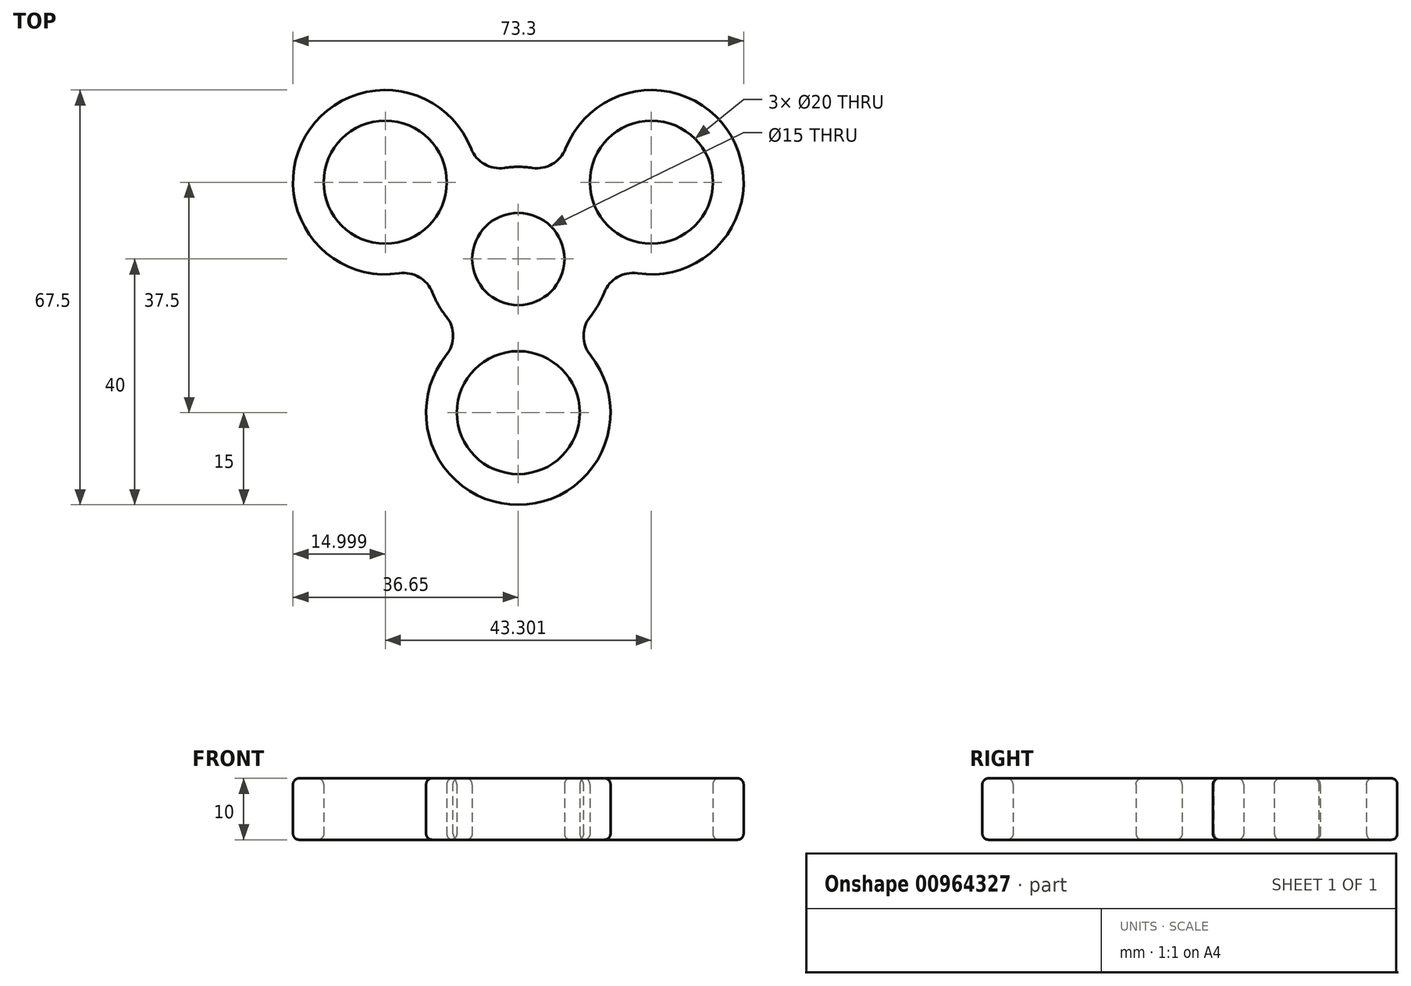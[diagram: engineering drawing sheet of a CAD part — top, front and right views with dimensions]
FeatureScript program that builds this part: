
annotation { "Feature Type Name" : "Feature", "Feature Type Description" : "" }
export const myFeature = defineFeature(function(context is Context, id is Id, definition is map)
    precondition{}
    {
        {
            var Q0;
            Q0=qCreatedBy(makeId("Top.planeOp"),FACE);
            var sketch = newSketch(context, id + "F0", { "sketchPlane" : qUnion([Q0])});
            skCircle(sketch, "E0", {"center": v(0, 0) * mm, "radius": 7.5 * mm});
            skCircle(sketch, "E1", {"center": v(0, 0) * mm, "radius": 15 * mm});
            skLineSegment(sketch, "E2", {"start": v(0, 0) * mm, "end": v(0, -25) * mm, "construction": true});
            skCircle(sketch, "E3", {"center": v(0, -25) * mm, "radius": 15 * mm});
            skCircle(sketch, "E4", {"center": v(0, -25) * mm, "radius": 10 * mm});
            skCircle(sketch, "E5.1.0", {"center": v(21.65, 12.5) * mm, "radius": 15 * mm});
            skCircle(sketch, "E5.1.1", {"center": v(21.65, 12.5) * mm, "radius": 10 * mm});
            skCircle(sketch, "E5.2.0", {"center": v(-21.65, 12.5) * mm, "radius": 15 * mm});
            skCircle(sketch, "E5.2.1", {"center": v(-21.65, 12.5) * mm, "radius": 10 * mm});
            skSolve(sketch);
        }
        {
            var Q0;
            {var subQ3=sQuery(id+"F0.wireOp",EDGE,"E5.2.1");Q0=makeQuery(id+"F0.imprint","IMPRINT",FACE,{"disambiguationData":[TD([[makeQuery(id+"F0.imprint","IMPRINT",EDGE,{"derivedFrom":subQ3}),-1.0]])]});}
            var Q1;
            Q1=makeQuery(id+"F0.imprint","IMPRINT",FACE,{"disambiguationData":[TD([[makeQuery(id+"F0.imprint","IMPRINT",EDGE,{"derivedFrom":sQuery(id+"F0.wireOp",EDGE,"E0")}),-1.0]])]});
            var Q2;
            {var subQ0=sQuery(id+"F0.wireOp",EDGE,"E5.2.0");var subQ1=sQuery(id+"F0.wireOp",EDGE,"E1");var subQ2=makeQuery(id+"F0.imprint","INTERSECT",VERTEX,{"disambiguationData":[OD(0.0)],"derivedFrom":[subQ1,subQ0]});Q2=makeQuery(id+"F0.imprint","IMPRINT",FACE,{"disambiguationData":[TD([[makeQuery(id+"F0.imprint","IMPRINT",EDGE,{"disambiguationData":[TD([[subQ2,-1.0]])],"derivedFrom":subQ1}),1.0]])]});}
            var Q3;
            {var subQ0=sQuery(id+"F0.wireOp",EDGE,"E5.1.0");var subQ1=sQuery(id+"F0.wireOp",EDGE,"E1");var subQ2=makeQuery(id+"F0.imprint","INTERSECT",VERTEX,{"disambiguationData":[OD(0.0)],"derivedFrom":[subQ1,subQ0]});Q3=makeQuery(id+"F0.imprint","IMPRINT",FACE,{"disambiguationData":[TD([[makeQuery(id+"F0.imprint","IMPRINT",EDGE,{"disambiguationData":[TD([[subQ2,1.0]])],"derivedFrom":subQ1}),1.0]])]});}
            var Q4;
            {var subQ3=sQuery(id+"F0.wireOp",EDGE,"E5.1.1");Q4=makeQuery(id+"F0.imprint","IMPRINT",FACE,{"disambiguationData":[TD([[makeQuery(id+"F0.imprint","IMPRINT",EDGE,{"derivedFrom":subQ3}),-1.0]])]});}
            var Q5;
            {var subQ0=sQuery(id+"F0.wireOp",EDGE,"E3");var subQ1=sQuery(id+"F0.wireOp",EDGE,"E1");var subQ2=makeQuery(id+"F0.imprint","INTERSECT",VERTEX,{"disambiguationData":[OD(0.0)],"derivedFrom":[subQ1,subQ0]});Q5=makeQuery(id+"F0.imprint","IMPRINT",FACE,{"disambiguationData":[TD([[makeQuery(id+"F0.imprint","IMPRINT",EDGE,{"disambiguationData":[TD([[subQ2,-1.0]])],"derivedFrom":subQ1}),1.0]])]});}
            var Q6;
            {var subQ3=sQuery(id+"F0.wireOp",EDGE,"E4");Q6=makeQuery(id+"F0.imprint","IMPRINT",FACE,{"disambiguationData":[TD([[makeQuery(id+"F0.imprint","IMPRINT",EDGE,{"derivedFrom":subQ3}),-1.0]])]});}
            extrude(context, id + "F1", {"entities" : qUnion([Q0, Q1, Q2, Q3, Q4, Q5, Q6]), "depth" : 10 * mm, "offsetDistance" : 25 * mm});
        }
        {
            var Q0;
            {var subQ0=sQuery(id+"F0.wireOp",EDGE,"E5.1.0");var subQ1=sQuery(id+"F0.wireOp",EDGE,"E1");Q0=makeQuery(id+"F1.opExtrude","SWEPT_EDGE",EDGE,{"disambiguationData":[OSD([subQ1,subQ0]),TDD([makeQuery(id+"F0.imprint","INTERSECT",VERTEX,{"disambiguationData":[OD(1.0)],"derivedFrom":[subQ1,subQ0]})])]});}
            var Q1;
            {var subQ0=sQuery(id+"F0.wireOp",EDGE,"E3");var subQ1=sQuery(id+"F0.wireOp",EDGE,"E1");Q1=makeQuery(id+"F1.opExtrude","SWEPT_EDGE",EDGE,{"disambiguationData":[OSD([subQ1,subQ0]),TDD([makeQuery(id+"F0.imprint","INTERSECT",VERTEX,{"disambiguationData":[OD(1.0)],"derivedFrom":[subQ1,subQ0]})])]});}
            var Q2;
            {var subQ0=sQuery(id+"F0.wireOp",EDGE,"E3");var subQ1=sQuery(id+"F0.wireOp",EDGE,"E1");Q2=makeQuery(id+"F1.opExtrude","SWEPT_EDGE",EDGE,{"disambiguationData":[OSD([subQ1,subQ0]),TDD([makeQuery(id+"F0.imprint","INTERSECT",VERTEX,{"disambiguationData":[OD(0.0)],"derivedFrom":[subQ1,subQ0]})])]});}
            var Q3;
            {var subQ0=sQuery(id+"F0.wireOp",EDGE,"E5.2.0");var subQ1=sQuery(id+"F0.wireOp",EDGE,"E1");Q3=makeQuery(id+"F1.opExtrude","SWEPT_EDGE",EDGE,{"disambiguationData":[OSD([subQ1,subQ0]),TDD([makeQuery(id+"F0.imprint","INTERSECT",VERTEX,{"disambiguationData":[OD(1.0)],"derivedFrom":[subQ1,subQ0]})])]});}
            var Q4;
            {var subQ0=sQuery(id+"F0.wireOp",EDGE,"E5.2.0");var subQ1=sQuery(id+"F0.wireOp",EDGE,"E1");Q4=makeQuery(id+"F1.opExtrude","SWEPT_EDGE",EDGE,{"disambiguationData":[OSD([subQ1,subQ0]),TDD([makeQuery(id+"F0.imprint","INTERSECT",VERTEX,{"disambiguationData":[OD(0.0)],"derivedFrom":[subQ1,subQ0]})])]});}
            var Q5;
            {var subQ0=sQuery(id+"F0.wireOp",EDGE,"E5.1.0");var subQ1=sQuery(id+"F0.wireOp",EDGE,"E1");Q5=makeQuery(id+"F1.opExtrude","SWEPT_EDGE",EDGE,{"disambiguationData":[OSD([subQ1,subQ0]),TDD([makeQuery(id+"F0.imprint","INTERSECT",VERTEX,{"disambiguationData":[OD(0.0)],"derivedFrom":[subQ1,subQ0]})])]});}
            fillet(context, id + "F2", {"entities" : qUnion([Q0, Q1, Q2, Q3, Q4, Q5]), "radius" : 5 * mm, "tangentPropagation" : true, "allowEdgeOverflow" : false});
        }
        {
            var Q0;
            Q0=makeQuery(id+"F1.opExtrude","CAP_EDGE",EDGE,{"disambiguationData":[OSD([sQuery(id+"F0.wireOp",EDGE,"E3")])],"isStart":true});
            var Q1;
            Q1=makeQuery(id+"F1.opExtrude","CAP_EDGE",EDGE,{"disambiguationData":[OSD([sQuery(id+"F0.wireOp",EDGE,"E5.1.0")])],"isStart":true});
            var Q2;
            Q2=makeQuery(id+"F1.opExtrude","CAP_EDGE",EDGE,{"disambiguationData":[OSD([sQuery(id+"F0.wireOp",EDGE,"E5.1.0")])],"isStart":false});
            var Q3;
            Q3=makeQuery(id+"F1.opExtrude","CAP_EDGE",EDGE,{"disambiguationData":[OSD([sQuery(id+"F0.wireOp",EDGE,"E5.2.0")])],"isStart":true});
            var Q4;
            Q4=makeQuery(id+"F1.opExtrude","CAP_EDGE",EDGE,{"disambiguationData":[OSD([sQuery(id+"F0.wireOp",EDGE,"E5.2.0")])],"isStart":false});
            var Q5;
            {var subQ0=sQuery(id+"F0.wireOp",EDGE,"E1");Q5=makeQuery(id+"F1.opExtrude","CAP_EDGE",EDGE,{"disambiguationData":[OSD([subQ0]),TDD([makeQuery(id+"F0.imprint","IMPRINT",EDGE,{"disambiguationData":[TD([[makeQuery(id+"F0.imprint","INTERSECT",VERTEX,{"disambiguationData":[OD(1.0)],"derivedFrom":[subQ0,sQuery(id+"F0.wireOp",EDGE,"E3")]}),-1.0]])],"derivedFrom":subQ0})])],"isStart":true});}
            var Q6;
            Q6=makeQuery(id+"F1.opExtrude","CAP_EDGE",EDGE,{"disambiguationData":[OSD([sQuery(id+"F0.wireOp",EDGE,"E5.2.1")])],"isStart":false});
            var Q7;
            Q7=makeQuery(id+"F1.opExtrude","CAP_EDGE",EDGE,{"disambiguationData":[OSD([sQuery(id+"F0.wireOp",EDGE,"E5.2.1")])],"isStart":true});
            var Q8;
            Q8=makeQuery(id+"F1.opExtrude","CAP_EDGE",EDGE,{"disambiguationData":[OSD([sQuery(id+"F0.wireOp",EDGE,"E4")])],"isStart":false});
            var Q9;
            Q9=makeQuery(id+"F1.opExtrude","CAP_EDGE",EDGE,{"disambiguationData":[OSD([sQuery(id+"F0.wireOp",EDGE,"E5.1.1")])],"isStart":true});
            var Q10;
            {var subQ0=sQuery(id+"F0.wireOp",EDGE,"E1");Q10=makeQuery(id+"F1.opExtrude","CAP_EDGE",EDGE,{"disambiguationData":[OSD([subQ0]),TDD([makeQuery(id+"F0.imprint","IMPRINT",EDGE,{"disambiguationData":[TD([[makeQuery(id+"F0.imprint","INTERSECT",VERTEX,{"disambiguationData":[OD(1.0)],"derivedFrom":[subQ0,sQuery(id+"F0.wireOp",EDGE,"E3")]}),-1.0]])],"derivedFrom":subQ0})])],"isStart":false});}
            var Q11;
            Q11=makeQuery(id+"F1.opExtrude","CAP_EDGE",EDGE,{"disambiguationData":[OSD([sQuery(id+"F0.wireOp",EDGE,"E5.1.1")])],"isStart":false});
            var Q12;
            Q12=makeQuery(id+"F1.opExtrude","CAP_EDGE",EDGE,{"disambiguationData":[OSD([sQuery(id+"F0.wireOp",EDGE,"E3")])],"isStart":false});
            var Q13;
            {var subQ0=sQuery(id+"F0.wireOp",EDGE,"E5.2.0");var subQ1=sQuery(id+"F0.wireOp",EDGE,"E1");Q13=makeQuery(id+"F2.opFillet","BLEND_EDGE",EDGE,{"blendedFrom":[makeQuery(id+"F1.opExtrude","SWEPT_EDGE",EDGE,{"disambiguationData":[OSD([subQ1,subQ0]),TDD([makeQuery(id+"F0.imprint","INTERSECT",VERTEX,{"disambiguationData":[OD(1.0)],"derivedFrom":[subQ1,subQ0]})])]}),makeQuery(id+"F1.opExtrude","SWEPT_FACE",FACE,{"disambiguationData":[OSD([subQ0])]})],"blendedInto":[makeQuery(id+"F1.opExtrude","SWEPT_FACE",FACE,{"disambiguationData":[OSD([subQ0])]})]});}
            var Q14;
            {var subQ0=sQuery(id+"F0.wireOp",EDGE,"E3");var subQ1=sQuery(id+"F0.wireOp",EDGE,"E1");Q14=makeQuery(id+"F2.opFillet","BLEND_EDGE",EDGE,{"blendedFrom":[makeQuery(id+"F1.opExtrude","SWEPT_EDGE",EDGE,{"disambiguationData":[OSD([subQ1,subQ0]),TDD([makeQuery(id+"F0.imprint","INTERSECT",VERTEX,{"disambiguationData":[OD(1.0)],"derivedFrom":[subQ1,subQ0]})])]}),makeQuery(id+"F1.opExtrude","CAP_FACE",FACE,{"disambiguationData":[OSD([sQuery(id+"F0.wireOp",EDGE,"E0"),subQ1,subQ0,sQuery(id+"F0.wireOp",EDGE,"E4"),sQuery(id+"F0.wireOp",EDGE,"E5.1.0"),sQuery(id+"F0.wireOp",EDGE,"E5.1.1"),sQuery(id+"F0.wireOp",EDGE,"E5.2.0"),sQuery(id+"F0.wireOp",EDGE,"E5.2.1")])],"isStart":true})],"blendedInto":[makeQuery(id+"F1.opExtrude","CAP_FACE",FACE,{"disambiguationData":[OSD([sQuery(id+"F0.wireOp",EDGE,"E0"),subQ1,subQ0,sQuery(id+"F0.wireOp",EDGE,"E4"),sQuery(id+"F0.wireOp",EDGE,"E5.1.0"),sQuery(id+"F0.wireOp",EDGE,"E5.1.1"),sQuery(id+"F0.wireOp",EDGE,"E5.2.0"),sQuery(id+"F0.wireOp",EDGE,"E5.2.1")])],"isStart":true})]});}
            var Q15;
            {var subQ0=sQuery(id+"F0.wireOp",EDGE,"E3");var subQ1=sQuery(id+"F0.wireOp",EDGE,"E1");Q15=makeQuery(id+"F2.opFillet","BLEND_EDGE",EDGE,{"blendedFrom":[makeQuery(id+"F1.opExtrude","SWEPT_EDGE",EDGE,{"disambiguationData":[OSD([subQ1,subQ0]),TDD([makeQuery(id+"F0.imprint","INTERSECT",VERTEX,{"disambiguationData":[OD(1.0)],"derivedFrom":[subQ1,subQ0]})])]}),makeQuery(id+"F1.opExtrude","CAP_FACE",FACE,{"disambiguationData":[OSD([sQuery(id+"F0.wireOp",EDGE,"E0"),subQ1,subQ0,sQuery(id+"F0.wireOp",EDGE,"E4"),sQuery(id+"F0.wireOp",EDGE,"E5.1.0"),sQuery(id+"F0.wireOp",EDGE,"E5.1.1"),sQuery(id+"F0.wireOp",EDGE,"E5.2.0"),sQuery(id+"F0.wireOp",EDGE,"E5.2.1")])],"isStart":false})],"blendedInto":[makeQuery(id+"F1.opExtrude","CAP_FACE",FACE,{"disambiguationData":[OSD([sQuery(id+"F0.wireOp",EDGE,"E0"),subQ1,subQ0,sQuery(id+"F0.wireOp",EDGE,"E4"),sQuery(id+"F0.wireOp",EDGE,"E5.1.0"),sQuery(id+"F0.wireOp",EDGE,"E5.1.1"),sQuery(id+"F0.wireOp",EDGE,"E5.2.0"),sQuery(id+"F0.wireOp",EDGE,"E5.2.1")])],"isStart":false})]});}
            var Q16;
            {var subQ0=sQuery(id+"F0.wireOp",EDGE,"E3");var subQ1=sQuery(id+"F0.wireOp",EDGE,"E1");var subQ2=makeQuery(id+"F0.imprint","INTERSECT",VERTEX,{"disambiguationData":[OD(1.0)],"derivedFrom":[subQ1,subQ0]});Q16=makeQuery(id+"F2.opFillet","BLEND_EDGE",EDGE,{"blendedFrom":[makeQuery(id+"F1.opExtrude","SWEPT_EDGE",EDGE,{"disambiguationData":[OSD([subQ1,subQ0]),TDD([subQ2])]}),makeQuery(id+"F1.opExtrude","SWEPT_FACE",FACE,{"disambiguationData":[OSD([subQ1]),TDD([makeQuery(id+"F0.imprint","IMPRINT",EDGE,{"disambiguationData":[TD([[subQ2,-1.0]])],"derivedFrom":subQ1})])]})],"blendedInto":[makeQuery(id+"F1.opExtrude","SWEPT_FACE",FACE,{"disambiguationData":[OSD([subQ1]),TDD([makeQuery(id+"F0.imprint","IMPRINT",EDGE,{"disambiguationData":[TD([[subQ2,-1.0]])],"derivedFrom":subQ1})])]})]});}
            var Q17;
            {var subQ0=sQuery(id+"F0.wireOp",EDGE,"E3");var subQ1=sQuery(id+"F0.wireOp",EDGE,"E1");Q17=makeQuery(id+"F2.opFillet","BLEND_EDGE",EDGE,{"blendedFrom":[makeQuery(id+"F1.opExtrude","SWEPT_EDGE",EDGE,{"disambiguationData":[OSD([subQ1,subQ0]),TDD([makeQuery(id+"F0.imprint","INTERSECT",VERTEX,{"disambiguationData":[OD(1.0)],"derivedFrom":[subQ1,subQ0]})])]}),makeQuery(id+"F1.opExtrude","SWEPT_FACE",FACE,{"disambiguationData":[OSD([subQ0])]})],"blendedInto":[makeQuery(id+"F1.opExtrude","SWEPT_FACE",FACE,{"disambiguationData":[OSD([subQ0])]})]});}
            var Q18;
            {var subQ0=sQuery(id+"F0.wireOp",EDGE,"E5.1.0");var subQ1=sQuery(id+"F0.wireOp",EDGE,"E1");Q18=makeQuery(id+"F2.opFillet","BLEND_EDGE",EDGE,{"blendedFrom":[makeQuery(id+"F1.opExtrude","SWEPT_EDGE",EDGE,{"disambiguationData":[OSD([subQ1,subQ0]),TDD([makeQuery(id+"F0.imprint","INTERSECT",VERTEX,{"disambiguationData":[OD(1.0)],"derivedFrom":[subQ1,subQ0]})])]}),makeQuery(id+"F1.opExtrude","CAP_FACE",FACE,{"disambiguationData":[OSD([sQuery(id+"F0.wireOp",EDGE,"E0"),subQ1,sQuery(id+"F0.wireOp",EDGE,"E3"),sQuery(id+"F0.wireOp",EDGE,"E4"),subQ0,sQuery(id+"F0.wireOp",EDGE,"E5.1.1"),sQuery(id+"F0.wireOp",EDGE,"E5.2.0"),sQuery(id+"F0.wireOp",EDGE,"E5.2.1")])],"isStart":true})],"blendedInto":[makeQuery(id+"F1.opExtrude","CAP_FACE",FACE,{"disambiguationData":[OSD([sQuery(id+"F0.wireOp",EDGE,"E0"),subQ1,sQuery(id+"F0.wireOp",EDGE,"E3"),sQuery(id+"F0.wireOp",EDGE,"E4"),subQ0,sQuery(id+"F0.wireOp",EDGE,"E5.1.1"),sQuery(id+"F0.wireOp",EDGE,"E5.2.0"),sQuery(id+"F0.wireOp",EDGE,"E5.2.1")])],"isStart":true})]});}
            var Q19;
            {var subQ0=sQuery(id+"F0.wireOp",EDGE,"E1");var subQ1=sQuery(id+"F0.wireOp",EDGE,"E5.1.0");var subQ2=makeQuery(id+"F0.imprint","INTERSECT",VERTEX,{"disambiguationData":[OD(1.0)],"derivedFrom":[subQ0,subQ1]});Q19=makeQuery(id+"F2.opFillet","BLEND_EDGE",EDGE,{"blendedFrom":[makeQuery(id+"F1.opExtrude","SWEPT_EDGE",EDGE,{"disambiguationData":[OSD([subQ0,subQ1]),TDD([subQ2])]}),makeQuery(id+"F1.opExtrude","SWEPT_FACE",FACE,{"disambiguationData":[OSD([subQ0]),TDD([makeQuery(id+"F0.imprint","IMPRINT",EDGE,{"disambiguationData":[TD([[makeQuery(id+"F0.imprint","INTERSECT",VERTEX,{"disambiguationData":[OD(1.0)],"derivedFrom":[subQ0,sQuery(id+"F0.wireOp",EDGE,"E3")]}),-1.0]])],"derivedFrom":subQ0})])]})],"blendedInto":[makeQuery(id+"F1.opExtrude","SWEPT_FACE",FACE,{"disambiguationData":[OSD([subQ0]),TDD([makeQuery(id+"F0.imprint","IMPRINT",EDGE,{"disambiguationData":[TD([[makeQuery(id+"F0.imprint","INTERSECT",VERTEX,{"disambiguationData":[OD(1.0)],"derivedFrom":[subQ0,sQuery(id+"F0.wireOp",EDGE,"E3")]}),-1.0]])],"derivedFrom":subQ0})])]})]});}
            var Q20;
            {var subQ0=sQuery(id+"F0.wireOp",EDGE,"E5.1.0");var subQ1=sQuery(id+"F0.wireOp",EDGE,"E1");Q20=makeQuery(id+"F2.opFillet","BLEND_EDGE",EDGE,{"blendedFrom":[makeQuery(id+"F1.opExtrude","SWEPT_EDGE",EDGE,{"disambiguationData":[OSD([subQ1,subQ0]),TDD([makeQuery(id+"F0.imprint","INTERSECT",VERTEX,{"disambiguationData":[OD(1.0)],"derivedFrom":[subQ1,subQ0]})])]}),makeQuery(id+"F1.opExtrude","SWEPT_FACE",FACE,{"disambiguationData":[OSD([subQ0])]})],"blendedInto":[makeQuery(id+"F1.opExtrude","SWEPT_FACE",FACE,{"disambiguationData":[OSD([subQ0])]})]});}
            var Q21;
            {var subQ0=sQuery(id+"F0.wireOp",EDGE,"E1");Q21=makeQuery(id+"F1.opExtrude","CAP_EDGE",EDGE,{"disambiguationData":[OSD([subQ0]),TDD([makeQuery(id+"F0.imprint","IMPRINT",EDGE,{"disambiguationData":[TD([[makeQuery(id+"F0.imprint","INTERSECT",VERTEX,{"disambiguationData":[OD(0.0)],"derivedFrom":[subQ0,sQuery(id+"F0.wireOp",EDGE,"E5.1.0")]}),-1.0]])],"derivedFrom":subQ0})])],"isStart":true});}
            var Q22;
            Q22=makeQuery(id+"F1.opExtrude","CAP_EDGE",EDGE,{"disambiguationData":[OSD([sQuery(id+"F0.wireOp",EDGE,"E0")])],"isStart":false});
            var Q23;
            {var subQ0=sQuery(id+"F0.wireOp",EDGE,"E5.2.0");var subQ1=sQuery(id+"F0.wireOp",EDGE,"E1");Q23=makeQuery(id+"F2.opFillet","BLEND_EDGE",EDGE,{"blendedFrom":[makeQuery(id+"F1.opExtrude","SWEPT_EDGE",EDGE,{"disambiguationData":[OSD([subQ1,subQ0]),TDD([makeQuery(id+"F0.imprint","INTERSECT",VERTEX,{"disambiguationData":[OD(0.0)],"derivedFrom":[subQ1,subQ0]})])]}),makeQuery(id+"F1.opExtrude","SWEPT_FACE",FACE,{"disambiguationData":[OSD([subQ0])]})],"blendedInto":[makeQuery(id+"F1.opExtrude","SWEPT_FACE",FACE,{"disambiguationData":[OSD([subQ0])]})]});}
            var Q24;
            {var subQ0=sQuery(id+"F0.wireOp",EDGE,"E5.2.0");var subQ1=sQuery(id+"F0.wireOp",EDGE,"E1");Q24=makeQuery(id+"F2.opFillet","BLEND_EDGE",EDGE,{"blendedFrom":[makeQuery(id+"F1.opExtrude","SWEPT_EDGE",EDGE,{"disambiguationData":[OSD([subQ1,subQ0]),TDD([makeQuery(id+"F0.imprint","INTERSECT",VERTEX,{"disambiguationData":[OD(1.0)],"derivedFrom":[subQ1,subQ0]})])]}),makeQuery(id+"F1.opExtrude","CAP_FACE",FACE,{"disambiguationData":[OSD([sQuery(id+"F0.wireOp",EDGE,"E0"),subQ1,sQuery(id+"F0.wireOp",EDGE,"E3"),sQuery(id+"F0.wireOp",EDGE,"E4"),sQuery(id+"F0.wireOp",EDGE,"E5.1.0"),sQuery(id+"F0.wireOp",EDGE,"E5.1.1"),subQ0,sQuery(id+"F0.wireOp",EDGE,"E5.2.1")])],"isStart":false})],"blendedInto":[makeQuery(id+"F1.opExtrude","CAP_FACE",FACE,{"disambiguationData":[OSD([sQuery(id+"F0.wireOp",EDGE,"E0"),subQ1,sQuery(id+"F0.wireOp",EDGE,"E3"),sQuery(id+"F0.wireOp",EDGE,"E4"),sQuery(id+"F0.wireOp",EDGE,"E5.1.0"),sQuery(id+"F0.wireOp",EDGE,"E5.1.1"),subQ0,sQuery(id+"F0.wireOp",EDGE,"E5.2.1")])],"isStart":false})]});}
            var Q25;
            {var subQ0=sQuery(id+"F0.wireOp",EDGE,"E5.1.0");var subQ1=sQuery(id+"F0.wireOp",EDGE,"E1");Q25=makeQuery(id+"F2.opFillet","BLEND_EDGE",EDGE,{"blendedFrom":[makeQuery(id+"F1.opExtrude","SWEPT_EDGE",EDGE,{"disambiguationData":[OSD([subQ1,subQ0]),TDD([makeQuery(id+"F0.imprint","INTERSECT",VERTEX,{"disambiguationData":[OD(0.0)],"derivedFrom":[subQ1,subQ0]})])]}),makeQuery(id+"F1.opExtrude","CAP_FACE",FACE,{"disambiguationData":[OSD([sQuery(id+"F0.wireOp",EDGE,"E0"),subQ1,sQuery(id+"F0.wireOp",EDGE,"E3"),sQuery(id+"F0.wireOp",EDGE,"E4"),subQ0,sQuery(id+"F0.wireOp",EDGE,"E5.1.1"),sQuery(id+"F0.wireOp",EDGE,"E5.2.0"),sQuery(id+"F0.wireOp",EDGE,"E5.2.1")])],"isStart":true})],"blendedInto":[makeQuery(id+"F1.opExtrude","CAP_FACE",FACE,{"disambiguationData":[OSD([sQuery(id+"F0.wireOp",EDGE,"E0"),subQ1,sQuery(id+"F0.wireOp",EDGE,"E3"),sQuery(id+"F0.wireOp",EDGE,"E4"),subQ0,sQuery(id+"F0.wireOp",EDGE,"E5.1.1"),sQuery(id+"F0.wireOp",EDGE,"E5.2.0"),sQuery(id+"F0.wireOp",EDGE,"E5.2.1")])],"isStart":true})]});}
            var Q26;
            {var subQ0=sQuery(id+"F0.wireOp",EDGE,"E3");var subQ1=sQuery(id+"F0.wireOp",EDGE,"E1");Q26=makeQuery(id+"F2.opFillet","BLEND_EDGE",EDGE,{"blendedFrom":[makeQuery(id+"F1.opExtrude","SWEPT_EDGE",EDGE,{"disambiguationData":[OSD([subQ1,subQ0]),TDD([makeQuery(id+"F0.imprint","INTERSECT",VERTEX,{"disambiguationData":[OD(0.0)],"derivedFrom":[subQ1,subQ0]})])]}),makeQuery(id+"F1.opExtrude","SWEPT_FACE",FACE,{"disambiguationData":[OSD([subQ0])]})],"blendedInto":[makeQuery(id+"F1.opExtrude","SWEPT_FACE",FACE,{"disambiguationData":[OSD([subQ0])]})]});}
            var Q27;
            {var subQ0=sQuery(id+"F0.wireOp",EDGE,"E3");var subQ1=sQuery(id+"F0.wireOp",EDGE,"E1");Q27=makeQuery(id+"F2.opFillet","BLEND_EDGE",EDGE,{"blendedFrom":[makeQuery(id+"F1.opExtrude","SWEPT_EDGE",EDGE,{"disambiguationData":[OSD([subQ1,subQ0]),TDD([makeQuery(id+"F0.imprint","INTERSECT",VERTEX,{"disambiguationData":[OD(0.0)],"derivedFrom":[subQ1,subQ0]})])]}),makeQuery(id+"F1.opExtrude","CAP_FACE",FACE,{"disambiguationData":[OSD([sQuery(id+"F0.wireOp",EDGE,"E0"),subQ1,subQ0,sQuery(id+"F0.wireOp",EDGE,"E4"),sQuery(id+"F0.wireOp",EDGE,"E5.1.0"),sQuery(id+"F0.wireOp",EDGE,"E5.1.1"),sQuery(id+"F0.wireOp",EDGE,"E5.2.0"),sQuery(id+"F0.wireOp",EDGE,"E5.2.1")])],"isStart":true})],"blendedInto":[makeQuery(id+"F1.opExtrude","CAP_FACE",FACE,{"disambiguationData":[OSD([sQuery(id+"F0.wireOp",EDGE,"E0"),subQ1,subQ0,sQuery(id+"F0.wireOp",EDGE,"E4"),sQuery(id+"F0.wireOp",EDGE,"E5.1.0"),sQuery(id+"F0.wireOp",EDGE,"E5.1.1"),sQuery(id+"F0.wireOp",EDGE,"E5.2.0"),sQuery(id+"F0.wireOp",EDGE,"E5.2.1")])],"isStart":true})]});}
            var Q28;
            {var subQ0=sQuery(id+"F0.wireOp",EDGE,"E5.2.0");var subQ1=sQuery(id+"F0.wireOp",EDGE,"E1");Q28=makeQuery(id+"F2.opFillet","BLEND_EDGE",EDGE,{"blendedFrom":[makeQuery(id+"F1.opExtrude","SWEPT_EDGE",EDGE,{"disambiguationData":[OSD([subQ1,subQ0]),TDD([makeQuery(id+"F0.imprint","INTERSECT",VERTEX,{"disambiguationData":[OD(0.0)],"derivedFrom":[subQ1,subQ0]})])]}),makeQuery(id+"F1.opExtrude","CAP_FACE",FACE,{"disambiguationData":[OSD([sQuery(id+"F0.wireOp",EDGE,"E0"),subQ1,sQuery(id+"F0.wireOp",EDGE,"E3"),sQuery(id+"F0.wireOp",EDGE,"E4"),sQuery(id+"F0.wireOp",EDGE,"E5.1.0"),sQuery(id+"F0.wireOp",EDGE,"E5.1.1"),subQ0,sQuery(id+"F0.wireOp",EDGE,"E5.2.1")])],"isStart":false})],"blendedInto":[makeQuery(id+"F1.opExtrude","CAP_FACE",FACE,{"disambiguationData":[OSD([sQuery(id+"F0.wireOp",EDGE,"E0"),subQ1,sQuery(id+"F0.wireOp",EDGE,"E3"),sQuery(id+"F0.wireOp",EDGE,"E4"),sQuery(id+"F0.wireOp",EDGE,"E5.1.0"),sQuery(id+"F0.wireOp",EDGE,"E5.1.1"),subQ0,sQuery(id+"F0.wireOp",EDGE,"E5.2.1")])],"isStart":false})]});}
            var Q29;
            Q29=makeQuery(id+"F1.opExtrude","CAP_EDGE",EDGE,{"disambiguationData":[OSD([sQuery(id+"F0.wireOp",EDGE,"E0")])],"isStart":true});
            var Q30;
            Q30=makeQuery(id+"F1.opExtrude","CAP_EDGE",EDGE,{"disambiguationData":[OSD([sQuery(id+"F0.wireOp",EDGE,"E4")])],"isStart":true});
            var Q31;
            {var subQ0=sQuery(id+"F0.wireOp",EDGE,"E1");Q31=makeQuery(id+"F1.opExtrude","CAP_EDGE",EDGE,{"disambiguationData":[OSD([subQ0]),TDD([makeQuery(id+"F0.imprint","IMPRINT",EDGE,{"disambiguationData":[TD([[makeQuery(id+"F0.imprint","INTERSECT",VERTEX,{"disambiguationData":[OD(0.0)],"derivedFrom":[subQ0,sQuery(id+"F0.wireOp",EDGE,"E5.1.0")]}),-1.0]])],"derivedFrom":subQ0})])],"isStart":false});}
            var Q32;
            {var subQ0=sQuery(id+"F0.wireOp",EDGE,"E5.1.0");var subQ1=sQuery(id+"F0.wireOp",EDGE,"E1");Q32=makeQuery(id+"F2.opFillet","BLEND_EDGE",EDGE,{"blendedFrom":[makeQuery(id+"F1.opExtrude","SWEPT_EDGE",EDGE,{"disambiguationData":[OSD([subQ1,subQ0]),TDD([makeQuery(id+"F0.imprint","INTERSECT",VERTEX,{"disambiguationData":[OD(1.0)],"derivedFrom":[subQ1,subQ0]})])]}),makeQuery(id+"F1.opExtrude","CAP_FACE",FACE,{"disambiguationData":[OSD([sQuery(id+"F0.wireOp",EDGE,"E0"),subQ1,sQuery(id+"F0.wireOp",EDGE,"E3"),sQuery(id+"F0.wireOp",EDGE,"E4"),subQ0,sQuery(id+"F0.wireOp",EDGE,"E5.1.1"),sQuery(id+"F0.wireOp",EDGE,"E5.2.0"),sQuery(id+"F0.wireOp",EDGE,"E5.2.1")])],"isStart":false})],"blendedInto":[makeQuery(id+"F1.opExtrude","CAP_FACE",FACE,{"disambiguationData":[OSD([sQuery(id+"F0.wireOp",EDGE,"E0"),subQ1,sQuery(id+"F0.wireOp",EDGE,"E3"),sQuery(id+"F0.wireOp",EDGE,"E4"),subQ0,sQuery(id+"F0.wireOp",EDGE,"E5.1.1"),sQuery(id+"F0.wireOp",EDGE,"E5.2.0"),sQuery(id+"F0.wireOp",EDGE,"E5.2.1")])],"isStart":false})]});}
            var Q33;
            {var subQ0=sQuery(id+"F0.wireOp",EDGE,"E3");var subQ1=sQuery(id+"F0.wireOp",EDGE,"E1");Q33=makeQuery(id+"F2.opFillet","BLEND_EDGE",EDGE,{"blendedFrom":[makeQuery(id+"F1.opExtrude","SWEPT_EDGE",EDGE,{"disambiguationData":[OSD([subQ1,subQ0]),TDD([makeQuery(id+"F0.imprint","INTERSECT",VERTEX,{"disambiguationData":[OD(0.0)],"derivedFrom":[subQ1,subQ0]})])]}),makeQuery(id+"F1.opExtrude","CAP_FACE",FACE,{"disambiguationData":[OSD([sQuery(id+"F0.wireOp",EDGE,"E0"),subQ1,subQ0,sQuery(id+"F0.wireOp",EDGE,"E4"),sQuery(id+"F0.wireOp",EDGE,"E5.1.0"),sQuery(id+"F0.wireOp",EDGE,"E5.1.1"),sQuery(id+"F0.wireOp",EDGE,"E5.2.0"),sQuery(id+"F0.wireOp",EDGE,"E5.2.1")])],"isStart":false})],"blendedInto":[makeQuery(id+"F1.opExtrude","CAP_FACE",FACE,{"disambiguationData":[OSD([sQuery(id+"F0.wireOp",EDGE,"E0"),subQ1,subQ0,sQuery(id+"F0.wireOp",EDGE,"E4"),sQuery(id+"F0.wireOp",EDGE,"E5.1.0"),sQuery(id+"F0.wireOp",EDGE,"E5.1.1"),sQuery(id+"F0.wireOp",EDGE,"E5.2.0"),sQuery(id+"F0.wireOp",EDGE,"E5.2.1")])],"isStart":false})]});}
            var Q34;
            {var subQ0=sQuery(id+"F0.wireOp",EDGE,"E5.1.0");var subQ1=sQuery(id+"F0.wireOp",EDGE,"E1");Q34=makeQuery(id+"F2.opFillet","BLEND_EDGE",EDGE,{"blendedFrom":[makeQuery(id+"F1.opExtrude","SWEPT_EDGE",EDGE,{"disambiguationData":[OSD([subQ1,subQ0]),TDD([makeQuery(id+"F0.imprint","INTERSECT",VERTEX,{"disambiguationData":[OD(0.0)],"derivedFrom":[subQ1,subQ0]})])]}),makeQuery(id+"F1.opExtrude","CAP_FACE",FACE,{"disambiguationData":[OSD([sQuery(id+"F0.wireOp",EDGE,"E0"),subQ1,sQuery(id+"F0.wireOp",EDGE,"E3"),sQuery(id+"F0.wireOp",EDGE,"E4"),subQ0,sQuery(id+"F0.wireOp",EDGE,"E5.1.1"),sQuery(id+"F0.wireOp",EDGE,"E5.2.0"),sQuery(id+"F0.wireOp",EDGE,"E5.2.1")])],"isStart":false})],"blendedInto":[makeQuery(id+"F1.opExtrude","CAP_FACE",FACE,{"disambiguationData":[OSD([sQuery(id+"F0.wireOp",EDGE,"E0"),subQ1,sQuery(id+"F0.wireOp",EDGE,"E3"),sQuery(id+"F0.wireOp",EDGE,"E4"),subQ0,sQuery(id+"F0.wireOp",EDGE,"E5.1.1"),sQuery(id+"F0.wireOp",EDGE,"E5.2.0"),sQuery(id+"F0.wireOp",EDGE,"E5.2.1")])],"isStart":false})]});}
            var Q35;
            {var subQ0=sQuery(id+"F0.wireOp",EDGE,"E5.2.0");var subQ1=sQuery(id+"F0.wireOp",EDGE,"E1");Q35=makeQuery(id+"F2.opFillet","BLEND_EDGE",EDGE,{"blendedFrom":[makeQuery(id+"F1.opExtrude","SWEPT_EDGE",EDGE,{"disambiguationData":[OSD([subQ1,subQ0]),TDD([makeQuery(id+"F0.imprint","INTERSECT",VERTEX,{"disambiguationData":[OD(0.0)],"derivedFrom":[subQ1,subQ0]})])]}),makeQuery(id+"F1.opExtrude","CAP_FACE",FACE,{"disambiguationData":[OSD([sQuery(id+"F0.wireOp",EDGE,"E0"),subQ1,sQuery(id+"F0.wireOp",EDGE,"E3"),sQuery(id+"F0.wireOp",EDGE,"E4"),sQuery(id+"F0.wireOp",EDGE,"E5.1.0"),sQuery(id+"F0.wireOp",EDGE,"E5.1.1"),subQ0,sQuery(id+"F0.wireOp",EDGE,"E5.2.1")])],"isStart":true})],"blendedInto":[makeQuery(id+"F1.opExtrude","CAP_FACE",FACE,{"disambiguationData":[OSD([sQuery(id+"F0.wireOp",EDGE,"E0"),subQ1,sQuery(id+"F0.wireOp",EDGE,"E3"),sQuery(id+"F0.wireOp",EDGE,"E4"),sQuery(id+"F0.wireOp",EDGE,"E5.1.0"),sQuery(id+"F0.wireOp",EDGE,"E5.1.1"),subQ0,sQuery(id+"F0.wireOp",EDGE,"E5.2.1")])],"isStart":true})]});}
            var Q36;
            {var subQ0=sQuery(id+"F0.wireOp",EDGE,"E5.1.0");var subQ1=sQuery(id+"F0.wireOp",EDGE,"E1");Q36=makeQuery(id+"F2.opFillet","BLEND_EDGE",EDGE,{"blendedFrom":[makeQuery(id+"F1.opExtrude","SWEPT_EDGE",EDGE,{"disambiguationData":[OSD([subQ1,subQ0]),TDD([makeQuery(id+"F0.imprint","INTERSECT",VERTEX,{"disambiguationData":[OD(0.0)],"derivedFrom":[subQ1,subQ0]})])]}),makeQuery(id+"F1.opExtrude","SWEPT_FACE",FACE,{"disambiguationData":[OSD([subQ0])]})],"blendedInto":[makeQuery(id+"F1.opExtrude","SWEPT_FACE",FACE,{"disambiguationData":[OSD([subQ0])]})]});}
            var Q37;
            {var subQ0=sQuery(id+"F0.wireOp",EDGE,"E1");Q37=makeQuery(id+"F1.opExtrude","CAP_EDGE",EDGE,{"disambiguationData":[OSD([subQ0]),TDD([makeQuery(id+"F0.imprint","IMPRINT",EDGE,{"disambiguationData":[TD([[makeQuery(id+"F0.imprint","INTERSECT",VERTEX,{"disambiguationData":[OD(1.0)],"derivedFrom":[subQ0,sQuery(id+"F0.wireOp",EDGE,"E5.2.0")]}),-1.0]])],"derivedFrom":subQ0})])],"isStart":false});}
            var Q38;
            {var subQ0=sQuery(id+"F0.wireOp",EDGE,"E1");Q38=makeQuery(id+"F1.opExtrude","CAP_EDGE",EDGE,{"disambiguationData":[OSD([subQ0]),TDD([makeQuery(id+"F0.imprint","IMPRINT",EDGE,{"disambiguationData":[TD([[makeQuery(id+"F0.imprint","INTERSECT",VERTEX,{"disambiguationData":[OD(1.0)],"derivedFrom":[subQ0,sQuery(id+"F0.wireOp",EDGE,"E5.2.0")]}),-1.0]])],"derivedFrom":subQ0})])],"isStart":true});}
            var Q39;
            {var subQ0=sQuery(id+"F0.wireOp",EDGE,"E1");var subQ1=sQuery(id+"F0.wireOp",EDGE,"E3");var subQ2=makeQuery(id+"F0.imprint","INTERSECT",VERTEX,{"disambiguationData":[OD(0.0)],"derivedFrom":[subQ0,subQ1]});Q39=makeQuery(id+"F2.opFillet","BLEND_EDGE",EDGE,{"blendedFrom":[makeQuery(id+"F1.opExtrude","SWEPT_EDGE",EDGE,{"disambiguationData":[OSD([subQ0,subQ1]),TDD([subQ2])]}),makeQuery(id+"F1.opExtrude","SWEPT_FACE",FACE,{"disambiguationData":[OSD([subQ0]),TDD([makeQuery(id+"F0.imprint","IMPRINT",EDGE,{"disambiguationData":[TD([[makeQuery(id+"F0.imprint","INTERSECT",VERTEX,{"disambiguationData":[OD(1.0)],"derivedFrom":[subQ0,sQuery(id+"F0.wireOp",EDGE,"E5.2.0")]}),-1.0]])],"derivedFrom":subQ0})])]})],"blendedInto":[makeQuery(id+"F1.opExtrude","SWEPT_FACE",FACE,{"disambiguationData":[OSD([subQ0]),TDD([makeQuery(id+"F0.imprint","IMPRINT",EDGE,{"disambiguationData":[TD([[makeQuery(id+"F0.imprint","INTERSECT",VERTEX,{"disambiguationData":[OD(1.0)],"derivedFrom":[subQ0,sQuery(id+"F0.wireOp",EDGE,"E5.2.0")]}),-1.0]])],"derivedFrom":subQ0})])]})]});}
            var Q40;
            {var subQ0=sQuery(id+"F0.wireOp",EDGE,"E1");var subQ1=sQuery(id+"F0.wireOp",EDGE,"E5.2.0");var subQ2=makeQuery(id+"F0.imprint","INTERSECT",VERTEX,{"disambiguationData":[OD(0.0)],"derivedFrom":[subQ0,subQ1]});Q40=makeQuery(id+"F2.opFillet","BLEND_EDGE",EDGE,{"blendedFrom":[makeQuery(id+"F1.opExtrude","SWEPT_EDGE",EDGE,{"disambiguationData":[OSD([subQ0,subQ1]),TDD([subQ2])]}),makeQuery(id+"F1.opExtrude","SWEPT_FACE",FACE,{"disambiguationData":[OSD([subQ0]),TDD([makeQuery(id+"F0.imprint","IMPRINT",EDGE,{"disambiguationData":[TD([[makeQuery(id+"F0.imprint","INTERSECT",VERTEX,{"disambiguationData":[OD(0.0)],"derivedFrom":[subQ0,sQuery(id+"F0.wireOp",EDGE,"E5.1.0")]}),-1.0]])],"derivedFrom":subQ0})])]})],"blendedInto":[makeQuery(id+"F1.opExtrude","SWEPT_FACE",FACE,{"disambiguationData":[OSD([subQ0]),TDD([makeQuery(id+"F0.imprint","IMPRINT",EDGE,{"disambiguationData":[TD([[makeQuery(id+"F0.imprint","INTERSECT",VERTEX,{"disambiguationData":[OD(0.0)],"derivedFrom":[subQ0,sQuery(id+"F0.wireOp",EDGE,"E5.1.0")]}),-1.0]])],"derivedFrom":subQ0})])]})]});}
            var Q41;
            {var subQ0=sQuery(id+"F0.wireOp",EDGE,"E5.2.0");var subQ1=sQuery(id+"F0.wireOp",EDGE,"E1");var subQ2=makeQuery(id+"F0.imprint","INTERSECT",VERTEX,{"disambiguationData":[OD(1.0)],"derivedFrom":[subQ1,subQ0]});Q41=makeQuery(id+"F2.opFillet","BLEND_EDGE",EDGE,{"blendedFrom":[makeQuery(id+"F1.opExtrude","SWEPT_EDGE",EDGE,{"disambiguationData":[OSD([subQ1,subQ0]),TDD([subQ2])]}),makeQuery(id+"F1.opExtrude","SWEPT_FACE",FACE,{"disambiguationData":[OSD([subQ1]),TDD([makeQuery(id+"F0.imprint","IMPRINT",EDGE,{"disambiguationData":[TD([[subQ2,-1.0]])],"derivedFrom":subQ1})])]})],"blendedInto":[makeQuery(id+"F1.opExtrude","SWEPT_FACE",FACE,{"disambiguationData":[OSD([subQ1]),TDD([makeQuery(id+"F0.imprint","IMPRINT",EDGE,{"disambiguationData":[TD([[subQ2,-1.0]])],"derivedFrom":subQ1})])]})]});}
            var Q42;
            {var subQ0=sQuery(id+"F0.wireOp",EDGE,"E5.1.0");var subQ1=sQuery(id+"F0.wireOp",EDGE,"E1");var subQ2=makeQuery(id+"F0.imprint","INTERSECT",VERTEX,{"disambiguationData":[OD(0.0)],"derivedFrom":[subQ1,subQ0]});Q42=makeQuery(id+"F2.opFillet","BLEND_EDGE",EDGE,{"blendedFrom":[makeQuery(id+"F1.opExtrude","SWEPT_EDGE",EDGE,{"disambiguationData":[OSD([subQ1,subQ0]),TDD([subQ2])]}),makeQuery(id+"F1.opExtrude","SWEPT_FACE",FACE,{"disambiguationData":[OSD([subQ1]),TDD([makeQuery(id+"F0.imprint","IMPRINT",EDGE,{"disambiguationData":[TD([[subQ2,-1.0]])],"derivedFrom":subQ1})])]})],"blendedInto":[makeQuery(id+"F1.opExtrude","SWEPT_FACE",FACE,{"disambiguationData":[OSD([subQ1]),TDD([makeQuery(id+"F0.imprint","IMPRINT",EDGE,{"disambiguationData":[TD([[subQ2,-1.0]])],"derivedFrom":subQ1})])]})]});}
            var Q43;
            {var subQ0=sQuery(id+"F0.wireOp",EDGE,"E5.2.0");var subQ1=sQuery(id+"F0.wireOp",EDGE,"E1");Q43=makeQuery(id+"F2.opFillet","BLEND_EDGE",EDGE,{"blendedFrom":[makeQuery(id+"F1.opExtrude","SWEPT_EDGE",EDGE,{"disambiguationData":[OSD([subQ1,subQ0]),TDD([makeQuery(id+"F0.imprint","INTERSECT",VERTEX,{"disambiguationData":[OD(1.0)],"derivedFrom":[subQ1,subQ0]})])]}),makeQuery(id+"F1.opExtrude","CAP_FACE",FACE,{"disambiguationData":[OSD([sQuery(id+"F0.wireOp",EDGE,"E0"),subQ1,sQuery(id+"F0.wireOp",EDGE,"E3"),sQuery(id+"F0.wireOp",EDGE,"E4"),sQuery(id+"F0.wireOp",EDGE,"E5.1.0"),sQuery(id+"F0.wireOp",EDGE,"E5.1.1"),subQ0,sQuery(id+"F0.wireOp",EDGE,"E5.2.1")])],"isStart":true})],"blendedInto":[makeQuery(id+"F1.opExtrude","CAP_FACE",FACE,{"disambiguationData":[OSD([sQuery(id+"F0.wireOp",EDGE,"E0"),subQ1,sQuery(id+"F0.wireOp",EDGE,"E3"),sQuery(id+"F0.wireOp",EDGE,"E4"),sQuery(id+"F0.wireOp",EDGE,"E5.1.0"),sQuery(id+"F0.wireOp",EDGE,"E5.1.1"),subQ0,sQuery(id+"F0.wireOp",EDGE,"E5.2.1")])],"isStart":true})]});}
            fillet(context, id + "F3", {"entities" : qUnion([Q0, Q1, Q2, Q3, Q4, Q5, Q6, Q7, Q8, Q9, Q10, Q11, Q12, Q13, Q14, Q15, Q16, Q17, Q18, Q19, Q20, Q21, Q22, Q23, Q24, Q25, Q26, Q27, Q28, Q29, Q30, Q31, Q32, Q33, Q34, Q35, Q36, Q37, Q38, Q39, Q40, Q41, Q42, Q43]), "radius" : 1 * mm, "tangentPropagation" : true, "allowEdgeOverflow" : false});
        }
    });
